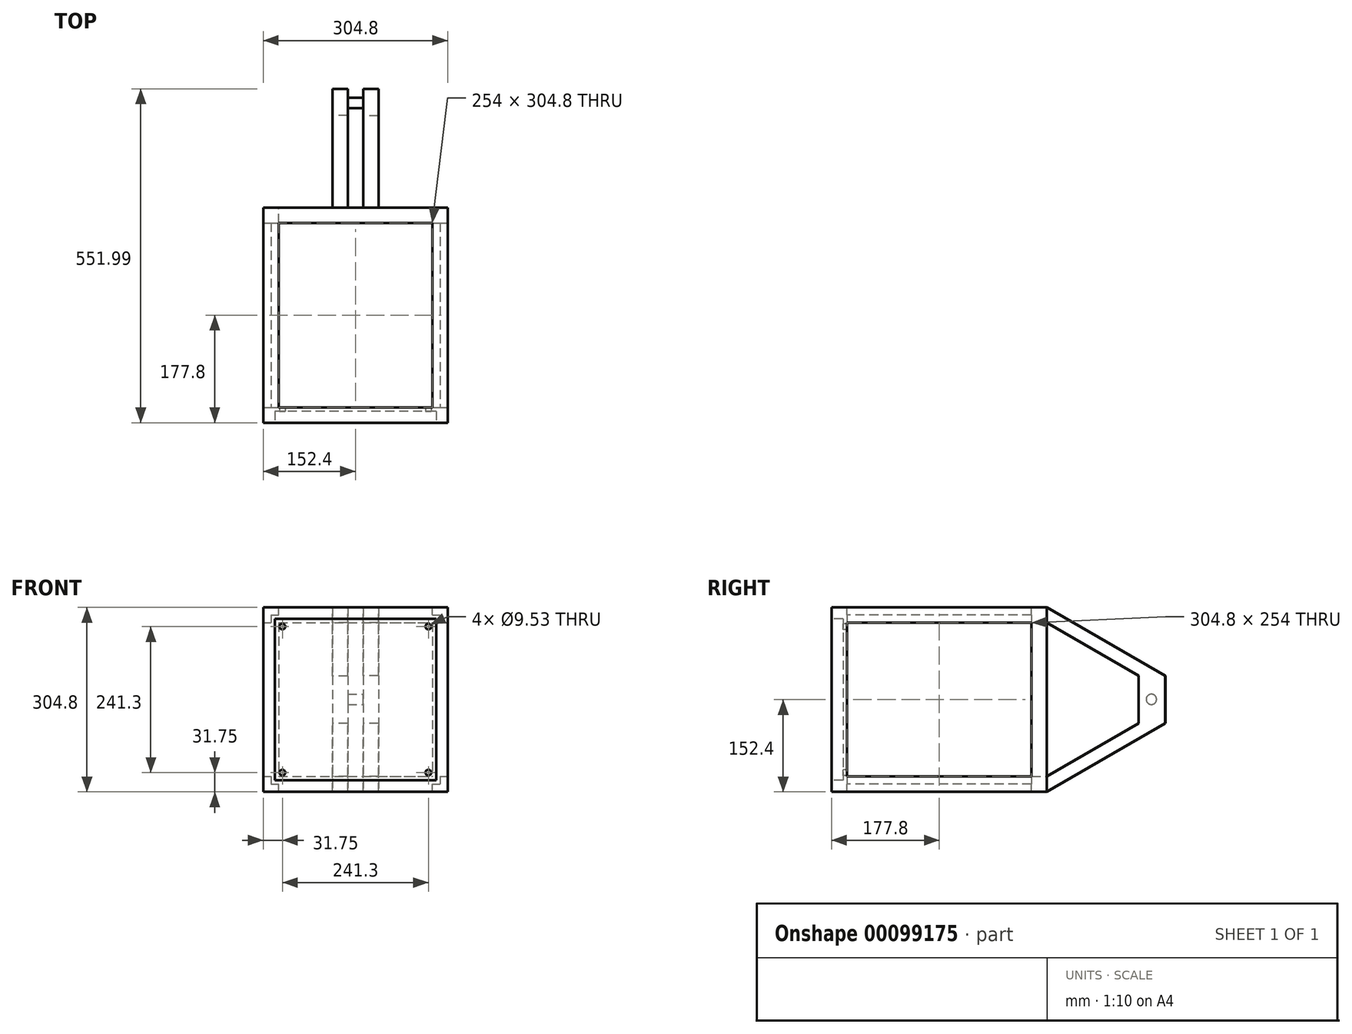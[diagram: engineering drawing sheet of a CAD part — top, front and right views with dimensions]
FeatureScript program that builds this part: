
annotation { "Feature Type Name" : "Feature", "Feature Type Description" : "" }
export const myFeature = defineFeature(function(context is Context, id is Id, definition is map)
    precondition{}
    {
        {
            var Q0;
            Q0=qCreatedBy(makeId("Top.planeOp"),FACE);
            var sketch = newSketch(context, id + "F0", { "sketchPlane" : qUnion([Q0])});
            skLineSegment(sketch, "E0.bottom", {"start": v(0, 0) * mm, "end": v(304.8, 0) * mm});
            skLineSegment(sketch, "E0.top", {"start": v(0, 355.6) * mm, "end": v(304.8, 355.6) * mm});
            skLineSegment(sketch, "E0.left", {"start": v(0, 0) * mm, "end": v(0, 355.6) * mm});
            skLineSegment(sketch, "E0.right", {"start": v(304.8, 0) * mm, "end": v(304.8, 355.6) * mm});
            skSolve(sketch);
        }
        {
            var Q0;
            Q0=makeQuery(id+"F0.imprint","IMPRINT",FACE,{"disambiguationData":[TD([[makeQuery(id+"F0.imprint","IMPRINT",EDGE,{"derivedFrom":sQuery(id+"F0.wireOp",EDGE,"E0.bottom")}),1.0]])]});
            extrude(context, id + "F1", {"entities" : qUnion([Q0]), "depth" : 304.8 * mm});
        }
        {
            var Q0;
            Q0=makeQuery(id+"F1.opExtrude","CAP_FACE",FACE,{"disambiguationData":[OSD([sQuery(id+"F0.wireOp",EDGE,"E0.bottom"),sQuery(id+"F0.wireOp",EDGE,"E0.top"),sQuery(id+"F0.wireOp",EDGE,"E0.left"),sQuery(id+"F0.wireOp",EDGE,"E0.right")])],"isStart":false});
            var sketch = newSketch(context, id + "F2", { "sketchPlane" : qUnion([Q0])});
            skLineSegment(sketch, "E1", {"start": v(0, 0) * mm, "end": v(152.4, 0) * mm, "construction": true});
            skLineSegment(sketch, "E2", {"start": v(152.4, 0) * mm, "end": v(152.4, 177.8) * mm, "construction": true});
            skPoint(sketch, "E2.endSnap0", {"position": v(0, 177.8) * mm});
            skLineSegment(sketch, "E3.bottom", {"start": v(279.4, 330.2) * mm, "end": v(25.4, 330.2) * mm});
            skLineSegment(sketch, "E3.top", {"start": v(279.4, 25.4) * mm, "end": v(25.4, 25.4) * mm});
            skLineSegment(sketch, "E3.left", {"start": v(279.4, 330.2) * mm, "end": v(279.4, 25.4) * mm});
            skLineSegment(sketch, "E3.right", {"start": v(25.4, 330.2) * mm, "end": v(25.4, 25.4) * mm});
            skPoint(sketch, "E3.middle", {"position": v(152.4, 177.8) * mm});
            skSolve(sketch);
        }
        {
            var Q0;
            Q0=makeQuery(id+"F2.imprint","IMPRINT",FACE,{"disambiguationData":[TD([[makeQuery(id+"F2.imprint","IMPRINT",EDGE,{"derivedFrom":sQuery(id+"F2.wireOp",EDGE,"E3.bottom")}),1.0]])]});
            extrude(context, id + "F3", {"entities" : qUnion([Q0]), "operationType" : NewBodyOperationType.REMOVE, "endBound" : BoundingType.THROUGH_ALL, "oppositeDirection" : true, "depth" : 25.4 * mm});
        }
        {
            var Q0;
            Q0=makeQuery(id+"F1.opExtrude","SWEPT_FACE",FACE,{"disambiguationData":[OSD([sQuery(id+"F0.wireOp",EDGE,"E0.right")])]});
            var sketch = newSketch(context, id + "F4", { "sketchPlane" : qUnion([Q0])});
            skLineSegment(sketch, "E4", {"start": v(0, 0) * mm, "end": v(177.8, 0) * mm, "construction": true});
            skLineSegment(sketch, "E5", {"start": v(177.8, 0) * mm, "end": v(177.8, 152.4) * mm, "construction": true});
            skPoint(sketch, "E5.endSnap0", {"position": v(0, 152.4) * mm});
            skLineSegment(sketch, "E6.bottom", {"start": v(330.2, 279.4) * mm, "end": v(25.4, 279.4) * mm});
            skLineSegment(sketch, "E6.top", {"start": v(330.2, 25.4) * mm, "end": v(25.4, 25.4) * mm});
            skLineSegment(sketch, "E6.left", {"start": v(330.2, 279.4) * mm, "end": v(330.2, 25.4) * mm});
            skLineSegment(sketch, "E6.right", {"start": v(25.4, 279.4) * mm, "end": v(25.4, 25.4) * mm});
            skPoint(sketch, "E6.middle", {"position": v(177.8, 152.4) * mm});
            skSolve(sketch);
        }
        {
            var Q0;
            Q0=makeQuery(id+"F4.imprint","IMPRINT",FACE,{"disambiguationData":[TD([[makeQuery(id+"F4.imprint","IMPRINT",EDGE,{"derivedFrom":sQuery(id+"F4.wireOp",EDGE,"E6.bottom")}),1.0]])]});
            extrude(context, id + "F5", {"entities" : qUnion([Q0]), "operationType" : NewBodyOperationType.REMOVE, "endBound" : BoundingType.THROUGH_ALL, "oppositeDirection" : true, "depth" : 25.4 * mm});
        }
        {
            var Q0;
            Q0=makeQuery(id+"F1.opExtrude","SWEPT_FACE",FACE,{"disambiguationData":[OSD([sQuery(id+"F0.wireOp",EDGE,"E0.top")])]});
            var sketch = newSketch(context, id + "F6", { "sketchPlane" : qUnion([Q0])});
            skLineSegment(sketch, "E7", {"start": v(0, 0) * mm, "end": v(-152.4, 0) * mm, "construction": true});
            skLineSegment(sketch, "E8", {"start": v(-152.4, 0) * mm, "end": v(-152.4, 152.4) * mm, "construction": true});
            skPoint(sketch, "E8.endSnap0", {"position": v(0, 152.4) * mm});
            skLineSegment(sketch, "E9.bottom", {"start": v(-25.4, 279.4) * mm, "end": v(-279.4, 279.4) * mm});
            skLineSegment(sketch, "E9.top", {"start": v(-25.4, 25.4) * mm, "end": v(-279.4, 25.4) * mm});
            skLineSegment(sketch, "E9.left", {"start": v(-25.4, 279.4) * mm, "end": v(-25.4, 25.4) * mm});
            skLineSegment(sketch, "E9.right", {"start": v(-279.4, 279.4) * mm, "end": v(-279.4, 25.4) * mm});
            skPoint(sketch, "E9.middle", {"position": v(-152.4, 152.4) * mm});
            skSolve(sketch);
        }
        {
            var Q0;
            Q0=makeQuery(id+"F6.imprint","IMPRINT",FACE,{"disambiguationData":[TD([[makeQuery(id+"F6.imprint","IMPRINT",EDGE,{"derivedFrom":sQuery(id+"F6.wireOp",EDGE,"E9.bottom")}),1.0]])]});
            extrude(context, id + "F7", {"entities" : qUnion([Q0]), "operationType" : NewBodyOperationType.REMOVE, "oppositeDirection" : true, "depth" : 25.4 * mm});
        }
        {
            var Q0;
            Q0=makeQuery(id+"F1.opExtrude","SWEPT_FACE",FACE,{"disambiguationData":[OSD([sQuery(id+"F0.wireOp",EDGE,"E0.bottom")])]});
            var sketch = newSketch(context, id + "F8", { "sketchPlane" : qUnion([Q0])});
            skLineSegment(sketch, "E10", {"start": v(0, 0) * mm, "end": v(152.4, 0) * mm, "construction": true});
            skLineSegment(sketch, "E11", {"start": v(152.4, 0) * mm, "end": v(152.4, 152.4) * mm, "construction": true});
            skPoint(sketch, "E11.endSnap0", {"position": v(0, 152.4) * mm});
            skLineSegment(sketch, "E12.bottom", {"start": v(285.75, 285.75) * mm, "end": v(19.05, 285.75) * mm});
            skLineSegment(sketch, "E12.top", {"start": v(285.75, 19.05) * mm, "end": v(19.05, 19.05) * mm});
            skLineSegment(sketch, "E12.left", {"start": v(285.75, 285.75) * mm, "end": v(285.75, 19.05) * mm});
            skLineSegment(sketch, "E12.right", {"start": v(19.05, 285.75) * mm, "end": v(19.05, 19.05) * mm});
            skPoint(sketch, "E12.middle", {"position": v(152.4, 152.4) * mm});
            skSolve(sketch);
        }
        {
            var Q0;
            Q0=makeQuery(id+"F8.imprint","IMPRINT",FACE,{"disambiguationData":[TD([[makeQuery(id+"F8.imprint","IMPRINT",EDGE,{"derivedFrom":sQuery(id+"F8.wireOp",EDGE,"E12.bottom")}),1.0]])]});
            extrude(context, id + "F9", {"entities" : qUnion([Q0]), "operationType" : NewBodyOperationType.REMOVE, "oppositeDirection" : true, "depth" : 19.05 * mm});
        }
        {
            var Q0;
            Q0=makeQuery(id+"F5.boolean.opBoolean","MERGE",FACE,{"derivedFrom":[makeQuery(id+"F3.boolean.opBoolean","COPY",FACE,{"derivedFrom":makeQuery(id+"F3.opExtrude","SWEPT_FACE",FACE,{"disambiguationData":[OSD([sQuery(id+"F2.wireOp",EDGE,"E3.top")])]})}),makeQuery(id+"F5.opExtrude","SWEPT_FACE",FACE,{"disambiguationData":[OSD([sQuery(id+"F4.wireOp",EDGE,"E6.right")])]})]});
            var sketch = newSketch(context, id + "F10", { "sketchPlane" : qUnion([Q0])});
            skLineSegment(sketch, "E13", {"start": v(0, 0) * mm, "end": v(-152.4, 0) * mm, "construction": true});
            skLineSegment(sketch, "E14", {"start": v(-152.4, 0) * mm, "end": v(-152.4, 152.4) * mm, "construction": true});
            skPoint(sketch, "E14.endSnap0", {"position": v(0, 152.4) * mm});
            skLineSegment(sketch, "E15.bottom", {"start": v(-12.7, 292.1) * mm, "end": v(-292.1, 292.1) * mm});
            skLineSegment(sketch, "E15.top", {"start": v(-12.7, 12.7) * mm, "end": v(-292.1, 12.7) * mm});
            skLineSegment(sketch, "E15.left", {"start": v(-12.7, 292.1) * mm, "end": v(-12.7, 12.7) * mm});
            skLineSegment(sketch, "E15.right", {"start": v(-292.1, 292.1) * mm, "end": v(-292.1, 12.7) * mm});
            skPoint(sketch, "E15.middle", {"position": v(-152.4, 152.4) * mm});
            skSolve(sketch);
        }
        {
            var Q0;
            Q0 = qSketchRegion(id + "F10", true);
            extrude(context, id + "F11", {"entities" : qUnion([Q0]), "operationType" : NewBodyOperationType.REMOVE, "depth" : 304.8 * mm});
        }
        {
            var Q0;
            Q0=makeQuery(id+"F9.boolean.opBoolean","COPY",FACE,{"derivedFrom":makeQuery(id+"F9.opExtrude","CAP_FACE",FACE,{"disambiguationData":[OSD([sQuery(id+"F8.wireOp",EDGE,"E12.bottom"),sQuery(id+"F8.wireOp",EDGE,"E12.top"),sQuery(id+"F8.wireOp",EDGE,"E12.left"),sQuery(id+"F8.wireOp",EDGE,"E12.right")])],"isStart":false})});
            var sketch = newSketch(context, id + "F12", { "sketchPlane" : qUnion([Q0])});
            skLineSegment(sketch, "E16", {"start": v(0, 0) * mm, "end": v(12.7, 0) * mm, "construction": true});
            skLineSegment(sketch, "E17", {"start": v(12.7, 0) * mm, "end": v(12.7, 12.7) * mm, "construction": true});
            skLineSegment(sketch, "E18", {"start": v(12.7, 12.7) * mm, "end": v(31.75, 12.7) * mm, "construction": true});
            skLineSegment(sketch, "E19", {"start": v(31.75, 12.7) * mm, "end": v(31.75, 31.75) * mm, "construction": true});
            skCircle(sketch, "E20", {"center": v(31.75, 31.75) * mm, "radius": 4.76 * mm});
            skCircle(sketch, "E21.0.1.0", {"center": v(31.75, 273.05) * mm, "radius": 4.76 * mm});
            skCircle(sketch, "E21.1.0.0", {"center": v(273.05, 31.75) * mm, "radius": 4.76 * mm});
            skCircle(sketch, "E21.1.1.0", {"center": v(273.05, 273.05) * mm, "radius": 4.76 * mm});
            skLineSegment(sketch, "E21.direction1", {"start": v(31.75, 31.75) * mm, "end": v(273.05, 31.75) * mm, "construction": true});
            skLineSegment(sketch, "E21.direction2", {"start": v(31.75, 31.75) * mm, "end": v(31.75, 273.05) * mm, "construction": true});
            skSolve(sketch);
        }
        {
            var Q0;
            Q0=makeQuery(id+"F12.imprint","IMPRINT",FACE,{"disambiguationData":[TD([[makeQuery(id+"F12.imprint","IMPRINT",EDGE,{"derivedFrom":sQuery(id+"F12.wireOp",EDGE,"E21.0.1.0")}),1.0]])]});
            var Q1;
            Q1=makeQuery(id+"F12.imprint","IMPRINT",FACE,{"disambiguationData":[TD([[makeQuery(id+"F12.imprint","IMPRINT",EDGE,{"derivedFrom":sQuery(id+"F12.wireOp",EDGE,"E21.1.1.0")}),1.0]])]});
            var Q2;
            Q2=makeQuery(id+"F12.imprint","IMPRINT",FACE,{"disambiguationData":[TD([[makeQuery(id+"F12.imprint","IMPRINT",EDGE,{"derivedFrom":sQuery(id+"F12.wireOp",EDGE,"E21.1.0.0")}),1.0]])]});
            var Q3;
            Q3=makeQuery(id+"F12.imprint","IMPRINT",FACE,{"disambiguationData":[TD([[makeQuery(id+"F12.imprint","IMPRINT",EDGE,{"derivedFrom":sQuery(id+"F12.wireOp",EDGE,"E20")}),1.0]])]});
            extrude(context, id + "F13", {"entities" : qUnion([Q0, Q1, Q2, Q3]), "operationType" : NewBodyOperationType.REMOVE, "oppositeDirection" : true, "depth" : 6.35 * mm});
        }
        {
            var Q0;
            Q0=qCreatedBy(makeId("Right.planeOp"),FACE);
            cPlane(context, id + "F14", {"entities" : qUnion([Q0]), "cplaneType" : CPlaneType.OFFSET, "offset" : 127 * mm, "width" : 152.4 * mm, "height" : 152.4 * mm});
        }
        {
            var Q0;
            Q0=qCreatedBy(id+"F14.planeOp",FACE);
            var sketch = newSketch(context, id + "F15", { "sketchPlane" : qUnion([Q0])});
            skLineSegment(sketch, "E22", {"start": v(0, 0) * mm, "end": v(355.6, 0) * mm, "construction": true});
            skLineSegment(sketch, "E23", {"start": v(355.6, 0) * mm, "end": v(355.6, 25.4) * mm});
            skLineSegment(sketch, "E24", {"start": v(355.6, 25.4) * mm, "end": v(508, 113.39) * mm});
            skLineSegment(sketch, "E25", {"start": v(508, 113.39) * mm, "end": v(508, 191.41) * mm});
            skLineSegment(sketch, "E26", {"start": v(508, 191.41) * mm, "end": v(355.6, 279.4) * mm});
            skLineSegment(sketch, "E27", {"start": v(355.6, 279.4) * mm, "end": v(355.6, 304.8) * mm});
            skLineSegment(sketch, "E28", {"start": v(355.6, 304.8) * mm, "end": v(552, 191.41) * mm});
            skLineSegment(sketch, "E29", {"start": v(552, 191.41) * mm, "end": v(552, 113.39) * mm});
            skLineSegment(sketch, "E30", {"start": v(552, 113.39) * mm, "end": v(355.6, 0) * mm});
            skSolve(sketch);
        }
        {
            var Q0;
            Q0=makeQuery(id+"F15.imprint","IMPRINT",FACE,{"disambiguationData":[TD([[makeQuery(id+"F15.imprint","IMPRINT",EDGE,{"derivedFrom":sQuery(id+"F15.wireOp",EDGE,"E23")}),-1.0]])]});
            extrude(context, id + "F16", {"entities" : qUnion([Q0]), "operationType" : NewBodyOperationType.ADD, "endBound" : BoundingType.SYMMETRIC, "depth" : 25.4 * mm});
        }
        {
            var Q0;
            Q0=qCreatedBy(id+"F14.planeOp",FACE);
            cPlane(context, id + "F17", {"entities" : qUnion([Q0]), "cplaneType" : CPlaneType.OFFSET, "offset" : 50.8 * mm, "width" : 152.4 * mm, "height" : 152.4 * mm});
        }
        {
            var Q0;
            Q0=qCreatedBy(id+"F17.planeOp",FACE);
            var sketch = newSketch(context, id + "F18", { "sketchPlane" : qUnion([Q0])});
            skLineSegment(sketch, "E31", {"start": v(0, 0) * mm, "end": v(355.6, 0) * mm, "construction": true});
            skLineSegment(sketch, "E32", {"start": v(355.6, 0) * mm, "end": v(355.6, 25.4) * mm});
            skLineSegment(sketch, "E33", {"start": v(355.6, 25.4) * mm, "end": v(507.48, 113.09) * mm});
            skLineSegment(sketch, "E34", {"start": v(507.48, 113.09) * mm, "end": v(507.48, 191.71) * mm});
            skLineSegment(sketch, "E35", {"start": v(507.48, 191.71) * mm, "end": v(355.6, 279.4) * mm});
            skLineSegment(sketch, "E36", {"start": v(355.6, 279.4) * mm, "end": v(355.6, 304.8) * mm});
            skLineSegment(sketch, "E37", {"start": v(355.6, 304.8) * mm, "end": v(551.47, 191.71) * mm});
            skLineSegment(sketch, "E38", {"start": v(551.47, 191.71) * mm, "end": v(551.47, 113.09) * mm});
            skLineSegment(sketch, "E39", {"start": v(551.47, 113.09) * mm, "end": v(355.6, 0) * mm});
            skSolve(sketch);
        }
        {
            var Q0;
            Q0=makeQuery(id+"F18.imprint","IMPRINT",FACE,{"disambiguationData":[TD([[makeQuery(id+"F18.imprint","IMPRINT",EDGE,{"derivedFrom":sQuery(id+"F18.wireOp",EDGE,"E32")}),-1.0]])]});
            extrude(context, id + "F19", {"entities" : qUnion([Q0]), "operationType" : NewBodyOperationType.ADD, "endBound" : BoundingType.SYMMETRIC, "depth" : 25.4 * mm});
        }
        {
            var Q0;
            Q0=makeQuery(id+"F19.opExtrude","CAP_FACE",FACE,{"disambiguationData":[OSD([sQuery(id+"F18.wireOp",EDGE,"E32"),sQuery(id+"F18.wireOp",EDGE,"E33"),sQuery(id+"F18.wireOp",EDGE,"E34"),sQuery(id+"F18.wireOp",EDGE,"E35"),sQuery(id+"F18.wireOp",EDGE,"E36"),sQuery(id+"F18.wireOp",EDGE,"E37"),sQuery(id+"F18.wireOp",EDGE,"E38"),sQuery(id+"F18.wireOp",EDGE,"E39")])],"isStart":true});
            var sketch = newSketch(context, id + "F20", { "sketchPlane" : qUnion([Q0])});
            skCircle(sketch, "E40", {"center": v(-528.49, 152.8) * mm, "radius": 8.53 * mm});
            skSolve(sketch);
        }
        {
            var Q0;
            Q0=makeQuery(id+"F20.imprint","IMPRINT",FACE,{"disambiguationData":[TD([[makeQuery(id+"F20.imprint","IMPRINT",EDGE,{"derivedFrom":sQuery(id+"F20.wireOp",EDGE,"E40")}),1.0]])]});
            extrude(context, id + "F21", {"entities" : qUnion([Q0]), "operationType" : NewBodyOperationType.ADD, "depth" : 25.4 * mm});
        }
    });
